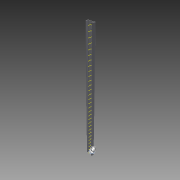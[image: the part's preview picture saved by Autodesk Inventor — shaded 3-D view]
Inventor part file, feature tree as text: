
AUTODESK INVENTOR PART (.ipt)
format: ipt  version: 2015 (Build 190159000, 159)  size: 450,560 bytes
history: native  units: in
note: dims shown in document units (in); Inventor stores cm internally (conversion verified against a paired STEP export)
features: other x34, boolean_combine x1, extrude x1, pattern_linear x1, imported_body x1, sketch x1
ambient origin geometry x8: Origin, YZ Plane, XZ Plane, XY Plane, X Axis, Y Axis, Z Axis, Center Point
bodies: Body1 (feature_tree)
feature tree (39):
  boolean_combine  "Combine1"
  other  "Linear Slide"
  other  "Work Axis1"
  extrude  "Extrusion1"  TaperAngle=0.0deg  [1 undecoded]
  pattern_linear  "Rectangular Pattern1"  Spacing1=0.0in  [1 undecoded]
  other  "bottom plane"
  other  "top plane"
  imported_body  "Base1"
  other  "Work Point1"
  other  "Work Axis2"
  sketch  "Sketch1"  dims[d0=11.811in d2=0.5in d4=0.0in d5=0.0in d6=0.0in d8=0.0in]
  other  "Work Axis46"
  other  "Work Axis47"
  other  "Work Axis48"
  other  "Work Axis49"
  other  "Work Axis50"
  other  "Work Axis51"
  other  "Work Axis52"
  other  "Work Axis53"
  other  "Work Axis54"
  other  "Work Axis55"
  other  "Work Axis56"
  other  "Work Axis57"
  other  "Work Axis69"
  other  "Work Axis70"
  other  "Work Axis71"
  other  "Work Axis72"
  other  "Work Axis73"
  other  "Work Axis74"
  other  "Work Axis75"
  other  "Work Axis76"
  other  "Work Axis77"
  other  "Work Axis78"
  other  "Work Axis90"
  other  "Work Axis96"
  other  "Work Axis97"
  other  "Work Axis98"
  other  "Work Axis99"
  other  "Work Axis100"
note: 2 required parameter values undecoded (feature->parameter linkage not recoverable at this tier; creation-order binding heuristic only, values carry confidence <= 0.55)
